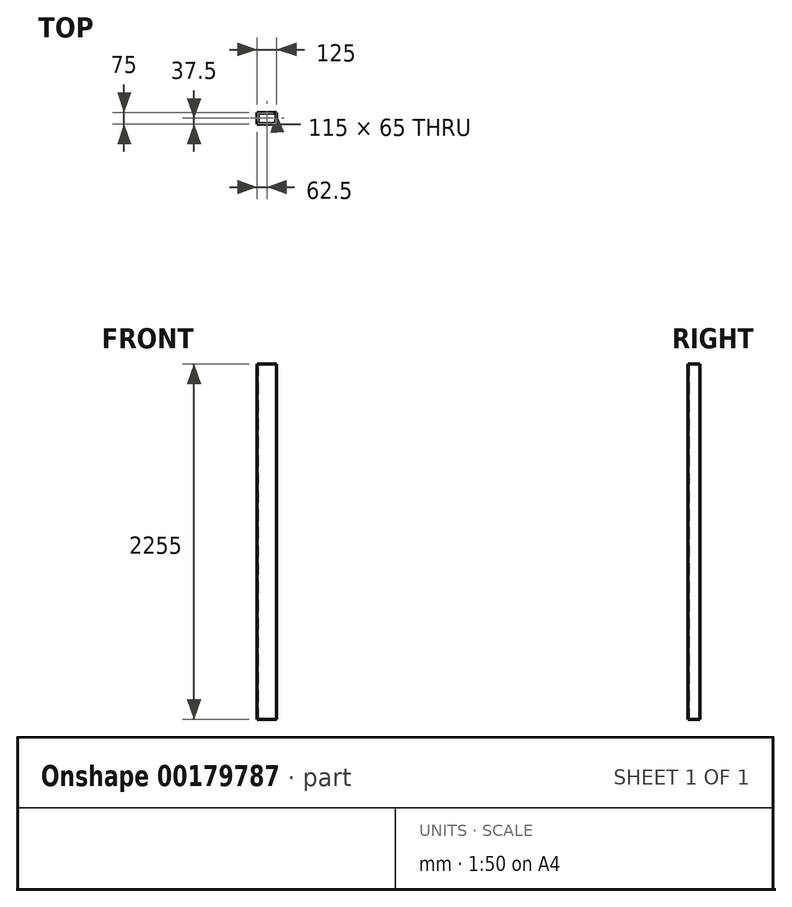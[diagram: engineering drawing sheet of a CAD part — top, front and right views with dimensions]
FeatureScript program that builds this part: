
annotation { "Feature Type Name" : "Feature", "Feature Type Description" : "" }
export const myFeature = defineFeature(function(context is Context, id is Id, definition is map)
    precondition{}
    {
        {
            var Q0;
            Q0=qCreatedBy(makeId("Top.planeOp"),FACE);
            var sketch = newSketch(context, id + "F0", { "sketchPlane" : qUnion([Q0])});
            skLineSegment(sketch, "E0.bottom", {"start": v(62.5, -37.5) * mm, "end": v(-62.5, -37.5) * mm});
            skLineSegment(sketch, "E0.top", {"start": v(62.5, 37.5) * mm, "end": v(-62.5, 37.5) * mm});
            skLineSegment(sketch, "E0.left", {"start": v(62.5, -37.5) * mm, "end": v(62.5, 37.5) * mm});
            skLineSegment(sketch, "E0.right", {"start": v(-62.5, -37.5) * mm, "end": v(-62.5, 37.5) * mm});
            skPoint(sketch, "E0.middle", {"position": v(0, 0) * mm});
            skLineSegment(sketch, "E1.bottom", {"start": v(57.5, -32.5) * mm, "end": v(-57.5, -32.5) * mm});
            skLineSegment(sketch, "E1.top", {"start": v(57.5, 32.5) * mm, "end": v(-57.5, 32.5) * mm});
            skLineSegment(sketch, "E1.left", {"start": v(57.5, -32.5) * mm, "end": v(57.5, 32.5) * mm});
            skLineSegment(sketch, "E1.right", {"start": v(-57.5, -32.5) * mm, "end": v(-57.5, 32.5) * mm});
            skSolve(sketch);
        }
        {
            var Q0;
            Q0=makeQuery(id+"F0.imprint","IMPRINT",FACE,{"disambiguationData":[TD([[makeQuery(id+"F0.imprint","IMPRINT",EDGE,{"derivedFrom":sQuery(id+"F0.wireOp",EDGE,"E0.bottom")}),-1.0]])]});
            extrude(context, id + "F1", {"entities" : qUnion([Q0]), "depth" : 2255 * mm});
        }
    });
